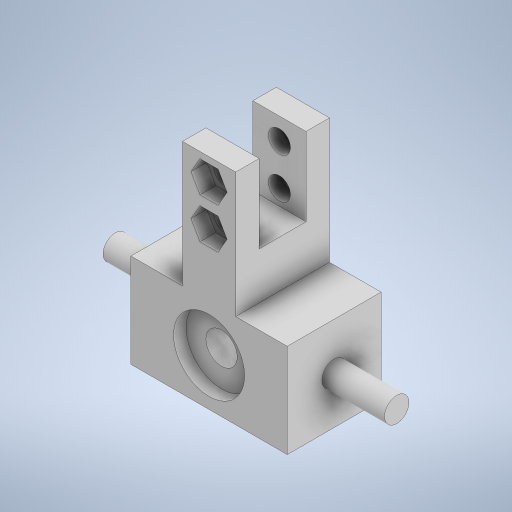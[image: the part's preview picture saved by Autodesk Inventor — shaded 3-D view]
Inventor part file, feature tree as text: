
AUTODESK INVENTOR PART (.ipt)
format: ipt  version: 2024 (Build 280153000, 153)  size: 345,088 bytes
history: native  units: in
note: dims shown in document units (in); Inventor stores cm internally (conversion verified against a paired STEP export)
features: sketch x11, extrude x9
ambient origin geometry x8: Origin, YZ Plane, XZ Plane, XY Plane, X Axis, Y Axis, Z Axis, Center Point
bodies: Solid1 (feature_tree)
feature tree (20):
  extrude  "Extrusion1"  Depth=1.1811in
  extrude  "Extrusion2"  Depth=1.9685in
  extrude  "Extrusion3"  Depth=0.6693in
  sketch  "Sketch4"  dims[d11=1.1811in d12=1.5748in d13=0.0in]
  extrude  "Extrusion4"  Depth=1.5748in TaperAngle=0.0deg
  sketch  "Sketch6"  dims[d17=0.8937in d18=0.1575in d19=0.0in]
  extrude  "Extrusion5"  TaperAngle=0.0deg  [1 undecoded]
  extrude  "Extrusion6"  Depth=0.1575in TaperAngle=0.0deg
  extrude  "Extrusion7"  Depth=0.9843in TaperAngle=0.0deg
  extrude  "Extrusion8"  Depth=0.9843in
  extrude  "Extrusion9"  Depth=0.1969in
  sketch  "Sketch1"  dims[d0=1.1811in d1=1.1811in]
  sketch  "Sketch2"  dims[d2=1.9685in d3=0.0in d5=0.3071in]
  sketch  "Sketch3"  dims[d6=0.7874in d7=2.7559in d8=0.0in d9=0.0in d10=0.6693in]
  sketch  "Sketch5"  dims[d14=0.3937in d15=0.0in d16=0.0in]
  sketch  "Sketch7"  dims[d20=0.5906in d21=0.9843in d22=0.0in]
  sketch  "Sketch8"  dims[d23=0.9843in d24=0.2756in]
  sketch  "Sketch9"  dims[d25=0.1969in d26=0.2756in]
  sketch  "Sketch10"  dims[d27=0.2756in]
  sketch  "Sketch11"  dims[d28=3.937in d29=0.0in d30=0.3937in d31=0.3937in d32=0.1969in d33=0.0in d34=0.4134in d35=0.4134in d36=0.1181in d37=0.0in]
note: 1 required parameter value undecoded (feature->parameter linkage not recoverable at this tier; creation-order binding heuristic only, values carry confidence <= 0.55)
